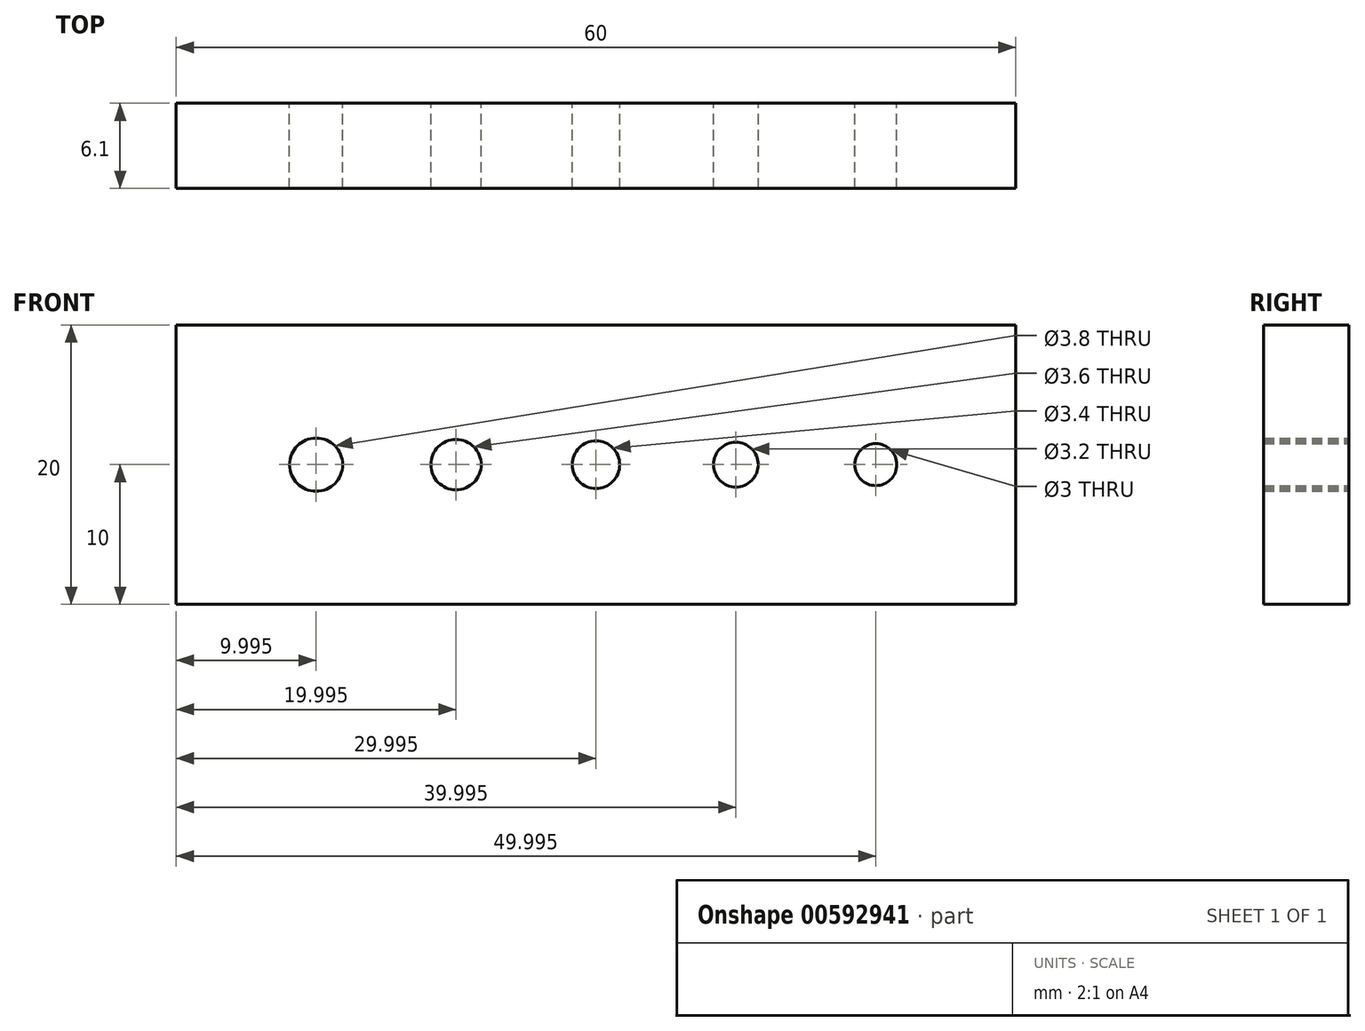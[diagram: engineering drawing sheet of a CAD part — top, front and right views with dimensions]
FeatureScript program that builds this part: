
annotation { "Feature Type Name" : "Feature", "Feature Type Description" : "" }
export const myFeature = defineFeature(function(context is Context, id is Id, definition is map)
    precondition{}
    {
        {
            var Q0;
            Q0=qCreatedBy(makeId("Front.planeOp"),FACE);
            var sketch = newSketch(context, id + "F0", { "sketchPlane" : qUnion([Q0])});
            skCircle(sketch, "E0", {"center": v(-38.07, 0) * mm, "radius": 1.9 * mm});
            skCircle(sketch, "E1", {"center": v(-28.07, 0) * mm, "radius": 1.8 * mm});
            skCircle(sketch, "E2", {"center": v(-18.07, 0) * mm, "radius": 1.7 * mm});
            skCircle(sketch, "E3", {"center": v(-8.07, 0) * mm, "radius": 1.6 * mm});
            skCircle(sketch, "E4", {"center": v(1.93, 0) * mm, "radius": 1.5 * mm});
            skLineSegment(sketch, "E5", {"start": v(-38.07, 0) * mm, "end": v(-28.07, 0) * mm, "construction": true});
            skLineSegment(sketch, "E6", {"start": v(-18.07, 0) * mm, "end": v(-8.07, 0) * mm, "construction": true});
            skLineSegment(sketch, "E7", {"start": v(-28.07, 0) * mm, "end": v(-18.07, 0) * mm, "construction": true});
            skLineSegment(sketch, "E8", {"start": v(-8.07, 0) * mm, "end": v(1.93, 0) * mm, "construction": true});
            skLineSegment(sketch, "E9.bottom", {"start": v(-48.07, 10) * mm, "end": v(11.93, 10) * mm});
            skLineSegment(sketch, "E9.top", {"start": v(-48.07, -10) * mm, "end": v(11.93, -10) * mm});
            skLineSegment(sketch, "E9.left", {"start": v(-48.07, 10) * mm, "end": v(-48.07, -10) * mm});
            skLineSegment(sketch, "E9.right", {"start": v(11.93, 10) * mm, "end": v(11.93, -10) * mm});
            skLineSegment(sketch, "E10", {"start": v(-38.07, 0) * mm, "end": v(-48.07, 0) * mm, "construction": true});
            skLineSegment(sketch, "E11", {"start": v(1.93, 0) * mm, "end": v(11.93, 0) * mm, "construction": true});
            skLineSegment(sketch, "E12", {"start": v(-48.07, 0) * mm, "end": v(-48.07, 10) * mm, "construction": true});
            skSolve(sketch);
        }
        {
            var Q0;
            Q0=makeQuery(id+"F0.imprint","IMPRINT",FACE,{"disambiguationData":[TD([[makeQuery(id+"F0.imprint","IMPRINT",EDGE,{"derivedFrom":sQuery(id+"F0.wireOp",EDGE,"E0")}),-1.0]])]});
            extrude(context, id + "F1", {"entities" : qUnion([Q0]), "depth" : 6.1 * mm, "offsetDistance" : 25 * mm});
        }
    });
